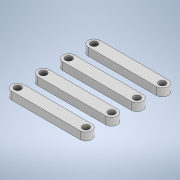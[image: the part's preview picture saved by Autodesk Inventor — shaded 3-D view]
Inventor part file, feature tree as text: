
AUTODESK INVENTOR PART (.ipt)
format: ipt  version: 2021 (Build 250183000, 183)  size: 168,960 bytes
history: native  units: mm
features: sketch x6, extrude x4
ambient origin geometry x8: Origin, YZ Plane, XZ Plane, XY Plane, X Axis, Y Axis, Z Axis, Center Point
bodies: Solid1 (feature_tree)
feature tree (10):
  extrude  "Extrusion1"  Depth=6.0mm
  extrude  "Extrusion2"  Depth=35.0mm
  sketch  "Sketch3"  dims[d4=6.0mm d5=4.0mm d6=0.0mm]
  extrude  "Extrusion3"  Depth=4.0mm TaperAngle=0.0deg
  extrude  "Extrusion4"  Depth=6.0mm
  sketch  "Sketch6"  dims[d10=6.0mm d11=4.0mm d12=0.0mm d13=13.0mm d14=3.5mm d15=6.0mm d16=3.5mm d17=6.0mm d18=4.0mm d19=0.0mm d20=13.0mm d21=6.0mm d22=3.5mm d23=6.0mm d24=3.5mm d25=4.0mm d26=0.0mm]
  sketch  "Sketch1"  dims[d0=3.5mm d1=6.0mm]
  sketch  "Sketch2"  dims[d2=35.0mm d3=3.5mm]
  sketch  "Sketch4"  dims[d7=6.0mm d8=3.5mm]
  sketch  "Sketch5"  dims[d9=3.5mm]
